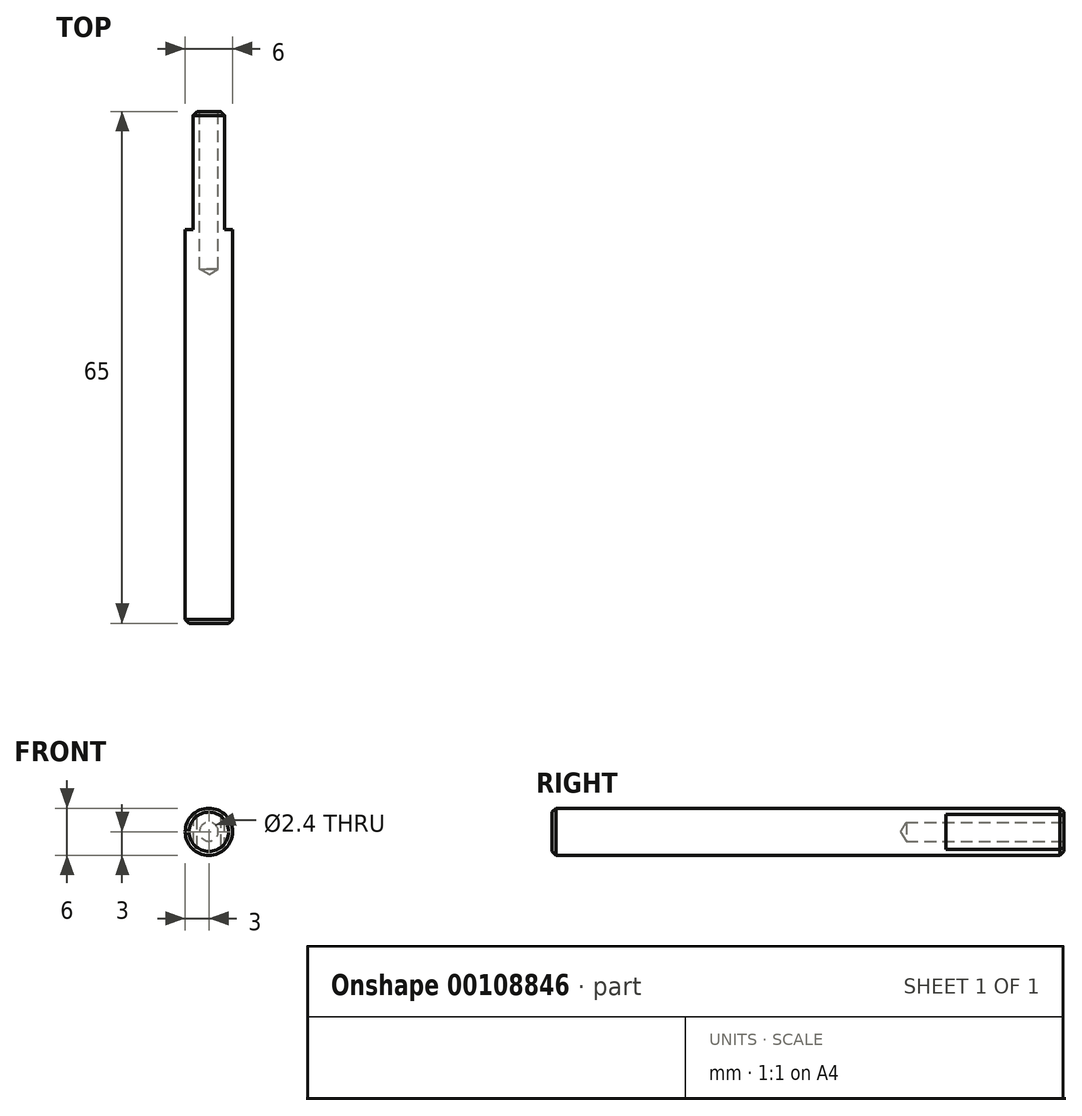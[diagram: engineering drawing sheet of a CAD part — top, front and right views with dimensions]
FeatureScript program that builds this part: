
annotation { "Feature Type Name" : "Feature", "Feature Type Description" : "" }
export const myFeature = defineFeature(function(context is Context, id is Id, definition is map)
    precondition{}
    {
        {
            var Q0;
            Q0=qCreatedBy(makeId("Front.planeOp"),FACE);
            var sketch = newSketch(context, id + "F0", { "sketchPlane" : qUnion([Q0])});
            skArc(sketch, "E0", {"start": v(-2, -2.24) * mm, "mid": v(0, -3) * mm, "end": v(2, -2.24) * mm});
            skLineSegment(sketch, "E1", {"start": v(-2, 2.24) * mm, "end": v(-2, -2.24) * mm});
            skLineSegment(sketch, "E2", {"start": v(0, 3.53) * mm, "end": v(0, -5.14) * mm, "construction": true});
            skLineSegment(sketch, "E3", {"start": v(2, 2.24) * mm, "end": v(2, -2.24) * mm});
            skArc(sketch, "E4.trimOffspring", {"start": v(2, 2.24) * mm, "mid": v(0, 3) * mm, "end": v(-2, 2.24) * mm});
            skSolve(sketch);
        }
        {
            var Q0;
            Q0 = qSketchRegion(id + "F0", true);
            extrude(context, id + "F1", {"entities" : qUnion([Q0]), "oppositeDirection" : true, "depth" : 15 * mm});
        }
        {
            var Q0;
            Q0=qCreatedBy(makeId("Front.planeOp"),FACE);
            var sketch = newSketch(context, id + "F2", { "sketchPlane" : qUnion([Q0])});
            skCircle(sketch, "E5", {"center": v(0, 0) * mm, "radius": 3 * mm});
            skSolve(sketch);
        }
        {
            var Q0;
            Q0=makeQuery(id+"F2.imprint","IMPRINT",FACE,{"disambiguationData":[TD([[makeQuery(id+"F2.imprint","IMPRINT",EDGE,{"derivedFrom":sQuery(id+"F2.wireOp",EDGE,"E5")}),1.0]])]});
            extrude(context, id + "F3", {"entities" : qUnion([Q0]), "operationType" : NewBodyOperationType.ADD, "depth" : 50 * mm});
        }
        {
            var Q0;
            Q0=makeQuery(id+"F3.opExtrude","CAP_EDGE",EDGE,{"disambiguationData":[OSD([sQuery(id+"F2.wireOp",EDGE,"E5")])],"isStart":false});
            var Q1;
            Q1=makeQuery(id+"F1.opExtrude","CAP_EDGE",EDGE,{"disambiguationData":[OSD([sQuery(id+"F0.wireOp",EDGE,"E4.trimOffspring")])],"isStart":false});
            var Q2;
            Q2=makeQuery(id+"F1.opExtrude","CAP_EDGE",EDGE,{"disambiguationData":[OSD([sQuery(id+"F0.wireOp",EDGE,"E1")])],"isStart":false});
            var Q3;
            Q3=makeQuery(id+"F1.opExtrude","CAP_EDGE",EDGE,{"disambiguationData":[OSD([sQuery(id+"F0.wireOp",EDGE,"E0")])],"isStart":false});
            var Q4;
            Q4=makeQuery(id+"F1.opExtrude","CAP_EDGE",EDGE,{"disambiguationData":[OSD([sQuery(id+"F0.wireOp",EDGE,"E3")])],"isStart":false});
            chamfer(context, id + "F4", {"entities" : qUnion([Q0, Q1, Q2, Q3, Q4]), "width" : 0.5 * mm, "tangentPropagation" : true});
        }
        {
            var Q0;
            Q0=makeQuery(id+"F1.opExtrude","CAP_FACE",FACE,{"disambiguationData":[OSD([sQuery(id+"F0.wireOp",EDGE,"E0"),sQuery(id+"F0.wireOp",EDGE,"E1"),sQuery(id+"F0.wireOp",EDGE,"E3"),sQuery(id+"F0.wireOp",EDGE,"E4.trimOffspring")])],"isStart":false});
            cPlane(context, id + "F5", {"entities" : qUnion([Q0]), "cplaneType" : CPlaneType.OFFSET, "offset" : 0 * mm, "width" : 150 * mm, "height" : 150 * mm});
        }
        {
            var Q0;
            Q0=qCreatedBy(id+"F5.planeOp",FACE);
            var sketch = newSketch(context, id + "F6", { "sketchPlane" : qUnion([Q0])});
            skPoint(sketch, "E6", {"position": v(0, 0) * mm});
            skSolve(sketch);
        }
        {
            var Q0;
            Q0=sQuery(id+"F6.wireOp",VERTEX,"E6");
            var Q1;
            Q1=makeQuery(id+"F1.opExtrude","SWEPT_BODY",BODY,{"disambiguationData":[OSD([sQuery(id+"F0.wireOp",EDGE,"E0"),sQuery(id+"F0.wireOp",EDGE,"E1"),sQuery(id+"F0.wireOp",EDGE,"E3"),sQuery(id+"F0.wireOp",EDGE,"E4.trimOffspring")])]});
            hole(context, id + "F7", {"style" : HoleStyle.SIMPLE, "endStyle" : HoleEndStyle.BLIND, "standardTappedOrClearance" : lookupTablePath({ "standard" : "ISO", "engagement" : "75%", "pitch" : "0.6 mm", "size" : "M3", "type" : "Tapped" }), "standardBlindInLast" : lookupTablePath({ "standard" : "ISO", "engagement" : "75%", "pitch" : "0.6 mm", "size" : "M3", "type" : "Tapped" }), "holeDiameter" : 2.4 * mm, "holeDepth" : 20 * mm, "startFromSketch" : true, "locations" : qUnion([Q0]), "scope" : qUnion([Q1])});
        }
    });
